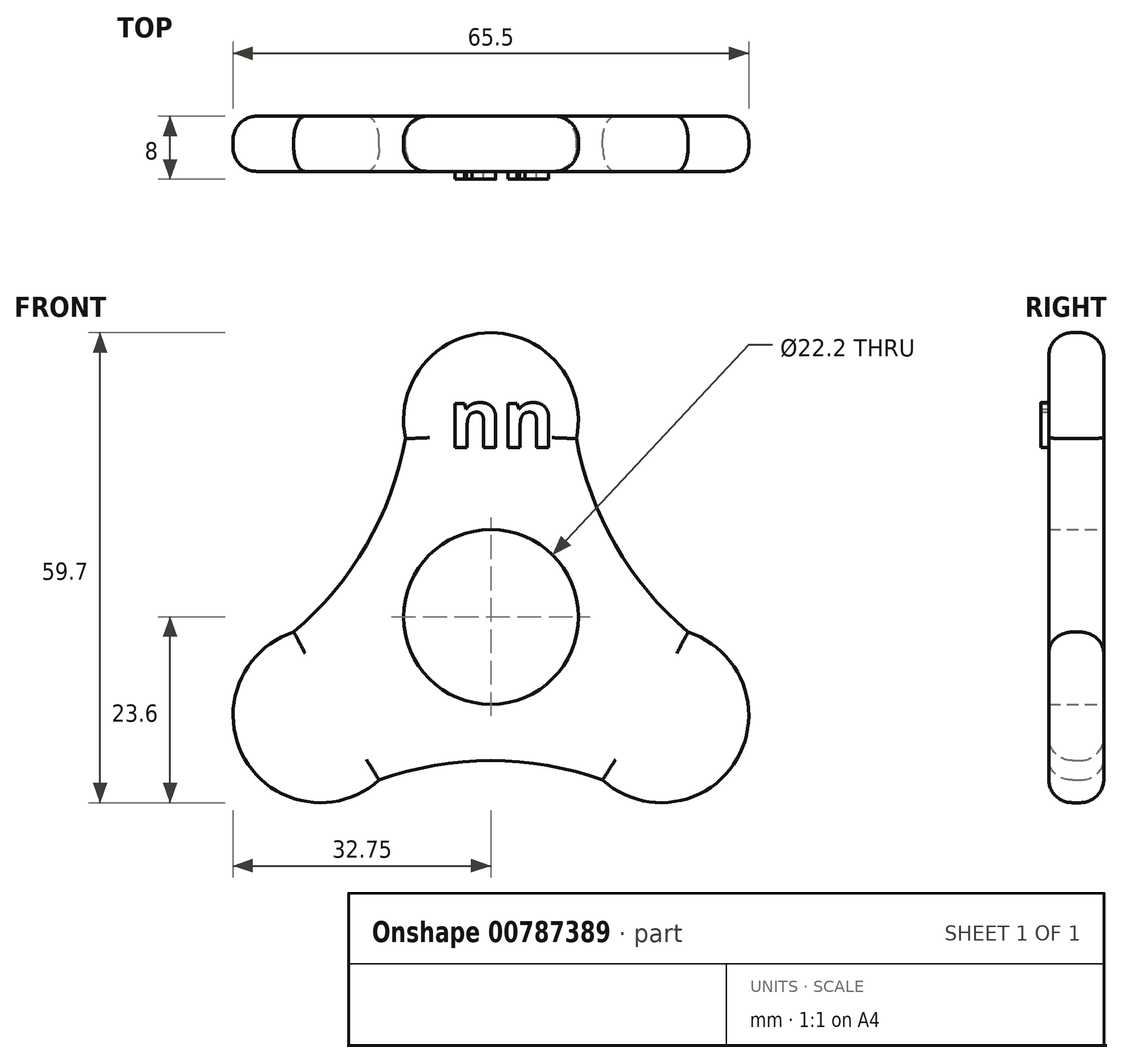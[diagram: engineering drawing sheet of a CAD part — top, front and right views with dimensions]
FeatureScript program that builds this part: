
annotation { "Feature Type Name" : "Feature", "Feature Type Description" : "" }
export const myFeature = defineFeature(function(context is Context, id is Id, definition is map)
    precondition{}
    {
        {
            var Q0;
            Q0=qCreatedBy(makeId("Front.planeOp"),FACE);
            var sketch = newSketch(context, id + "F0", { "sketchPlane" : qUnion([Q0])});
            skCircle(sketch, "E0", {"center": v(0, 0) * mm, "radius": 11.1 * mm});
            skArc(sketch, "E1", {"start": v(10.85, 22.66) * mm, "mid": v(0, 36.1) * mm, "end": v(-10.85, 22.66) * mm});
            skArc(sketch, "E2.1.0", {"start": v(-25.05, -1.93) * mm, "mid": v(-31.26, -18.05) * mm, "end": v(-14.2, -20.73) * mm});
            skArc(sketch, "E2.2.0", {"start": v(14.2, -20.73) * mm, "mid": v(31.26, -18.05) * mm, "end": v(25.05, -1.93) * mm});
            skArc(sketch, "E3", {"start": v(-25.05, -1.93) * mm, "mid": v(-15.81, 9.13) * mm, "end": v(-10.85, 22.66) * mm});
            skArc(sketch, "E4", {"start": v(10.85, 22.66) * mm, "mid": v(15.81, 9.13) * mm, "end": v(25.05, -1.93) * mm});
            skArc(sketch, "E5", {"start": v(14.2, -20.73) * mm, "mid": v(0, -18.26) * mm, "end": v(-14.2, -20.73) * mm});
            skSolve(sketch);
        }
        {
            var Q0;
            Q0 = qSketchRegion(id + "F0", true);
            extrude(context, id + "F1", {"entities" : qUnion([Q0]), "depth" : 7 * mm, "offsetDistance" : 25 * mm});
        }
        {
            var Q0;
            Q0=makeQuery(id+"F1.opExtrude","CAP_EDGE",EDGE,{"disambiguationData":[OSD([sQuery(id+"F0.wireOp",EDGE,"E1")])],"isStart":false});
            var Q1;
            Q1=makeQuery(id+"F1.opExtrude","CAP_EDGE",EDGE,{"disambiguationData":[OSD([sQuery(id+"F0.wireOp",EDGE,"E2.1.0")])],"isStart":false});
            var Q2;
            Q2=makeQuery(id+"F1.opExtrude","CAP_EDGE",EDGE,{"disambiguationData":[OSD([sQuery(id+"F0.wireOp",EDGE,"E2.2.0")])],"isStart":false});
            var Q3;
            Q3=makeQuery(id+"F1.opExtrude","CAP_EDGE",EDGE,{"disambiguationData":[OSD([sQuery(id+"F0.wireOp",EDGE,"E5")])],"isStart":false});
            var Q4;
            Q4=makeQuery(id+"F1.opExtrude","CAP_EDGE",EDGE,{"disambiguationData":[OSD([sQuery(id+"F0.wireOp",EDGE,"E4")])],"isStart":false});
            var Q5;
            Q5=makeQuery(id+"F1.opExtrude","CAP_EDGE",EDGE,{"disambiguationData":[OSD([sQuery(id+"F0.wireOp",EDGE,"E3")])],"isStart":false});
            fillet(context, id + "F2", {"entities" : qUnion([Q0, Q1, Q2, Q3, Q4, Q5]), "radius" : 3 * mm, "tangentPropagation" : true, "allowEdgeOverflow" : false});
        }
        {
            var Q0;
            Q0=makeQuery(id+"F1.opExtrude","CAP_EDGE",EDGE,{"disambiguationData":[OSD([sQuery(id+"F0.wireOp",EDGE,"E4")])],"isStart":true});
            var Q1;
            Q1=makeQuery(id+"F1.opExtrude","CAP_EDGE",EDGE,{"disambiguationData":[OSD([sQuery(id+"F0.wireOp",EDGE,"E2.2.0")])],"isStart":true});
            var Q2;
            Q2=makeQuery(id+"F1.opExtrude","CAP_EDGE",EDGE,{"disambiguationData":[OSD([sQuery(id+"F0.wireOp",EDGE,"E5")])],"isStart":true});
            var Q3;
            Q3=makeQuery(id+"F1.opExtrude","CAP_EDGE",EDGE,{"disambiguationData":[OSD([sQuery(id+"F0.wireOp",EDGE,"E2.1.0")])],"isStart":true});
            var Q4;
            Q4=makeQuery(id+"F1.opExtrude","CAP_EDGE",EDGE,{"disambiguationData":[OSD([sQuery(id+"F0.wireOp",EDGE,"E3")])],"isStart":true});
            var Q5;
            Q5=makeQuery(id+"F1.opExtrude","CAP_EDGE",EDGE,{"disambiguationData":[OSD([sQuery(id+"F0.wireOp",EDGE,"E1")])],"isStart":true});
            fillet(context, id + "F3", {"entities" : qUnion([Q0, Q1, Q2, Q3, Q4, Q5]), "radius" : 3 * mm, "tangentPropagation" : true, "allowEdgeOverflow" : false});
        }
        {
            var Q0;
            Q0=makeQuery(id+"F1.opExtrude","CAP_FACE",FACE,{"disambiguationData":[OSD([sQuery(id+"F0.wireOp",EDGE,"E0"),sQuery(id+"F0.wireOp",EDGE,"E1"),sQuery(id+"F0.wireOp",EDGE,"E2.1.0"),sQuery(id+"F0.wireOp",EDGE,"E2.2.0"),sQuery(id+"F0.wireOp",EDGE,"E3"),sQuery(id+"F0.wireOp",EDGE,"E4"),sQuery(id+"F0.wireOp",EDGE,"E5")])],"isStart":false});
            var sketch = newSketch(context, id + "F4", { "sketchPlane" : qUnion([Q0])});
            skText(sketch, "E6", { "text": "nn", "fontName": "OpenSans-Bold.ttf"});
            const initialGuessF4  = {"E6": [-0.00535, 0.02154, 1, 0, 0.00737]};
            skSetInitialGuess(sketch, initialGuessF4);
            skSolve(sketch);
        }
        {
            var Q0;
            Q0 = qSketchRegion(id + "F4", true);
            extrude(context, id + "F5", {"entities" : qUnion([Q0]), "operationType" : NewBodyOperationType.ADD, "depth" : 1 * mm, "offsetDistance" : 25 * mm});
        }
    });
